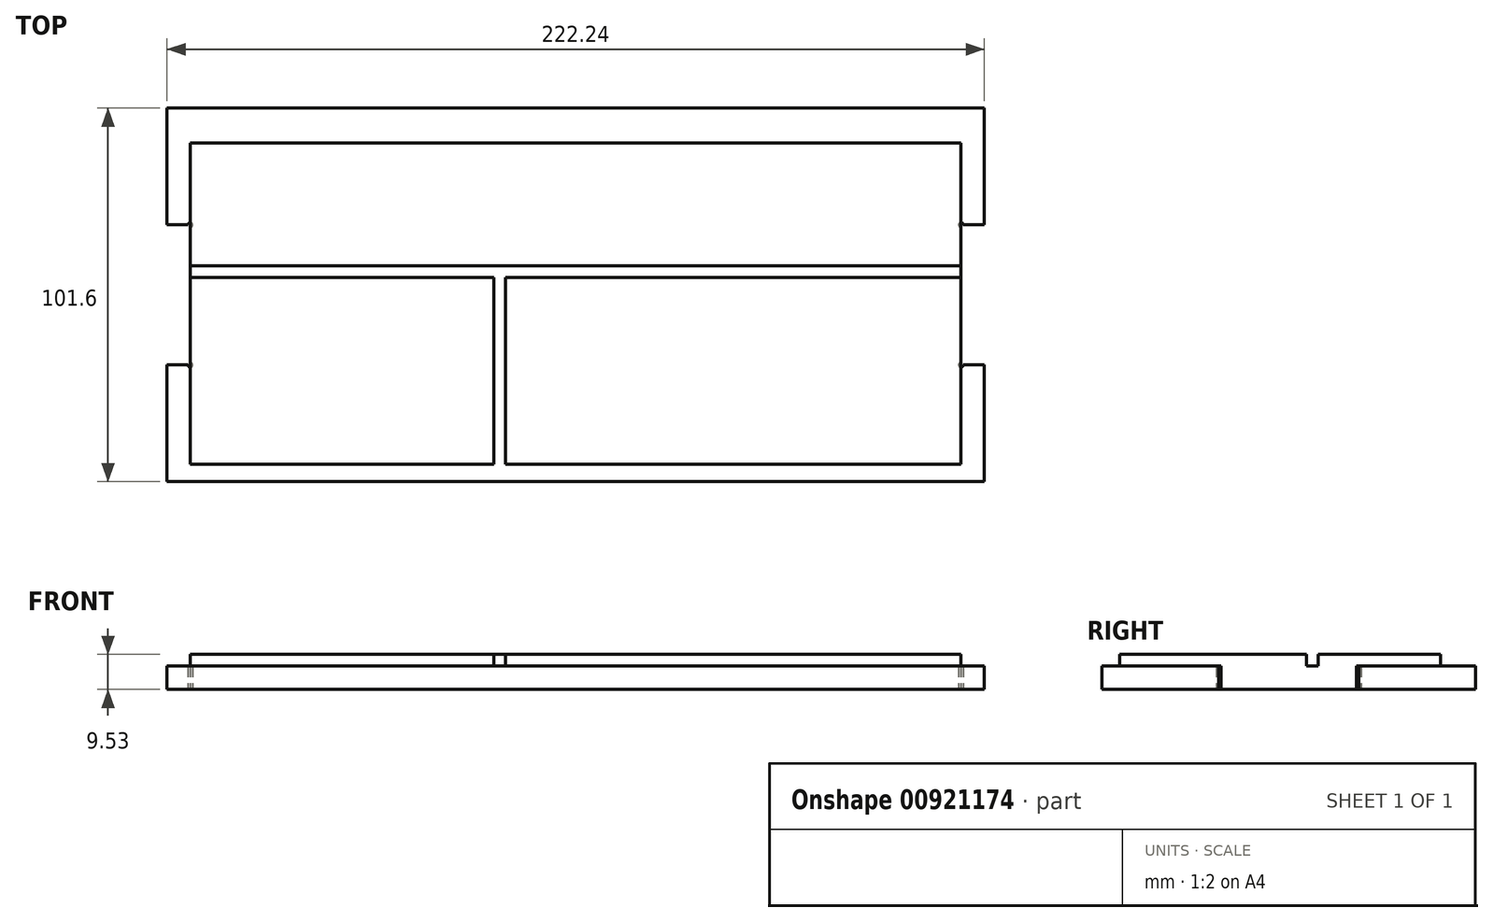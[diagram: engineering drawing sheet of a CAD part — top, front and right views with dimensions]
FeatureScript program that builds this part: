
annotation { "Feature Type Name" : "Feature", "Feature Type Description" : "" }
export const myFeature = defineFeature(function(context is Context, id is Id, definition is map)
    precondition{}
    {
        {
            var Q0;
            Q0=qCreatedBy(makeId("Top.planeOp"),FACE);
            var sketch = newSketch(context, id + "F0", { "sketchPlane" : qUnion([Q0])});
            skLineSegment(sketch, "E0.bottom", {"start": v(111.13, -50.8) * mm, "end": v(-111.12, -50.8) * mm});
            skLineSegment(sketch, "E0.top", {"start": v(111.12, 50.8) * mm, "end": v(-111.13, 50.8) * mm});
            skLineSegment(sketch, "E0.left", {"start": v(111.13, -50.8) * mm, "end": v(111.12, 50.8) * mm});
            skLineSegment(sketch, "E0.right", {"start": v(-111.12, -50.8) * mm, "end": v(-111.13, 50.8) * mm});
            skPoint(sketch, "E0.middle", {"position": v(0, 0) * mm});
            skSolve(sketch);
        }
        {
            var Q0;
            Q0=qSketchRegion(id+"F0",true);
            extrude(context, id + "F1", {"entities" : qUnion([Q0]), "depth" : 9.52 * mm, "offsetDistance" : 25.4 * mm});
        }
        {
            var Q0;
            Q0=makeQuery(id+"F1.opExtrude","CAP_FACE",FACE,{"disambiguationData":[OSD([sQuery(id+"F0.wireOp",EDGE,"E0.bottom"),sQuery(id+"F0.wireOp",EDGE,"E0.top"),sQuery(id+"F0.wireOp",EDGE,"E0.left"),sQuery(id+"F0.wireOp",EDGE,"E0.right")])],"isStart":false});
            var sketch = newSketch(context, id + "F2", { "sketchPlane" : qUnion([Q0])});
            skLineSegment(sketch, "E1.bottom", {"start": v(-111.13, 19.05) * mm, "end": v(-104.78, 19.05) * mm});
            skLineSegment(sketch, "E1.top", {"start": v(-111.13, -19.05) * mm, "end": v(-104.78, -19.05) * mm});
            skLineSegment(sketch, "E1.left", {"start": v(-111.13, 19.05) * mm, "end": v(-111.13, -19.05) * mm});
            skLineSegment(sketch, "E1.right", {"start": v(-104.78, 19.05) * mm, "end": v(-104.78, -19.05) * mm});
            skLineSegment(sketch, "E2.bottom", {"start": v(111.13, 19.05) * mm, "end": v(104.78, 19.05) * mm});
            skLineSegment(sketch, "E2.top", {"start": v(111.13, -19.05) * mm, "end": v(104.78, -19.05) * mm});
            skLineSegment(sketch, "E2.left", {"start": v(111.13, 19.05) * mm, "end": v(111.13, -19.05) * mm});
            skLineSegment(sketch, "E2.right", {"start": v(104.78, 19.05) * mm, "end": v(104.78, -19.05) * mm});
            skLineSegment(sketch, "E3", {"start": v(-111.13, 0) * mm, "end": v(111.12, 0) * mm, "construction": true});
            skSolve(sketch);
        }
        {
            var Q0;
            Q0=qSketchRegion(id+"F2",true);
            extrude(context, id + "F3", {"entities" : qUnion([Q0]), "operationType" : NewBodyOperationType.REMOVE, "endBound" : BoundingType.THROUGH_ALL, "oppositeDirection" : true, "depth" : 25.4 * mm, "offsetDistance" : 25.4 * mm});
        }
        {
            var Q0;
            Q0=makeQuery(id+"F1.opExtrude","CAP_FACE",FACE,{"disambiguationData":[OSD([sQuery(id+"F0.wireOp",EDGE,"E0.bottom"),sQuery(id+"F0.wireOp",EDGE,"E0.top"),sQuery(id+"F0.wireOp",EDGE,"E0.left"),sQuery(id+"F0.wireOp",EDGE,"E0.right")])],"isStart":false});
            var sketch = newSketch(context, id + "F4", { "sketchPlane" : qUnion([Q0])});
            skLineSegment(sketch, "E4", {"start": v(-104.78, 19.05) * mm, "end": v(-111.13, 19.05) * mm});
            skLineSegment(sketch, "E5", {"start": v(-111.13, 19.05) * mm, "end": v(-111.13, 50.8) * mm});
            skLineSegment(sketch, "E6", {"start": v(-111.13, 50.8) * mm, "end": v(111.12, 50.8) * mm});
            skLineSegment(sketch, "E7", {"start": v(111.12, 50.8) * mm, "end": v(111.12, 19.05) * mm});
            skLineSegment(sketch, "E8", {"start": v(111.12, 19.05) * mm, "end": v(104.78, 19.05) * mm});
            skLineSegment(sketch, "E9", {"start": v(104.78, 19.05) * mm, "end": v(104.78, 41.28) * mm});
            skLineSegment(sketch, "E10", {"start": v(104.78, 41.28) * mm, "end": v(-104.78, 41.28) * mm});
            skLineSegment(sketch, "E11", {"start": v(-104.78, 41.28) * mm, "end": v(-104.78, 19.05) * mm});
            skLineSegment(sketch, "E12", {"start": v(111.13, -19.05) * mm, "end": v(111.13, -50.8) * mm});
            skLineSegment(sketch, "E13", {"start": v(111.13, -50.8) * mm, "end": v(-111.12, -50.8) * mm});
            skLineSegment(sketch, "E14", {"start": v(-111.12, -50.8) * mm, "end": v(-111.12, -19.05) * mm});
            skLineSegment(sketch, "E15", {"start": v(-111.12, -19.05) * mm, "end": v(-104.78, -19.05) * mm});
            skLineSegment(sketch, "E16", {"start": v(-104.77, -19.05) * mm, "end": v(-104.77, -46.04) * mm});
            skLineSegment(sketch, "E17", {"start": v(-104.77, -46.04) * mm, "end": v(104.78, -46.04) * mm});
            skLineSegment(sketch, "E18", {"start": v(104.78, -46.04) * mm, "end": v(104.78, -19.05) * mm});
            skLineSegment(sketch, "E19", {"start": v(104.78, -19.05) * mm, "end": v(111.13, -19.05) * mm});
            skSolve(sketch);
        }
        {
            var Q0;
            Q0=makeQuery(id+"F4.imprint","IMPRINT",FACE,{"disambiguationData":[TD([[makeQuery(id+"F4.imprint","IMPRINT",EDGE,{"derivedFrom":sQuery(id+"F4.wireOp",EDGE,"E12")}),1.0]])]});
            var Q1;
            Q1=makeQuery(id+"F4.imprint","IMPRINT",FACE,{"disambiguationData":[TD([[makeQuery(id+"F4.imprint","IMPRINT",EDGE,{"derivedFrom":sQuery(id+"F4.wireOp",EDGE,"E4")}),1.0]])]});
            extrude(context, id + "F5", {"entities" : qUnion([Q0, Q1]), "operationType" : NewBodyOperationType.REMOVE, "oppositeDirection" : true, "depth" : 3.17 * mm, "offsetDistance" : 25.4 * mm});
        }
        {
            var Q0;
            Q0=makeQuery(id+"F1.opExtrude","CAP_FACE",FACE,{"disambiguationData":[OSD([sQuery(id+"F0.wireOp",EDGE,"E0.bottom"),sQuery(id+"F0.wireOp",EDGE,"E0.top"),sQuery(id+"F0.wireOp",EDGE,"E0.left"),sQuery(id+"F0.wireOp",EDGE,"E0.right")])],"isStart":false});
            var sketch = newSketch(context, id + "F6", { "sketchPlane" : qUnion([Q0])});
            skLineSegment(sketch, "E20.bottom", {"start": v(-104.78, 7.94) * mm, "end": v(104.78, 7.94) * mm});
            skLineSegment(sketch, "E20.top", {"start": v(-104.78, 4.76) * mm, "end": v(104.78, 4.76) * mm});
            skLineSegment(sketch, "E20.left", {"start": v(-104.78, 7.94) * mm, "end": v(-104.78, 4.76) * mm});
            skLineSegment(sketch, "E20.right", {"start": v(104.78, 7.94) * mm, "end": v(104.78, 4.76) * mm});
            skLineSegment(sketch, "E21", {"start": v(-19.05, 4.76) * mm, "end": v(-19.05, -46.04) * mm});
            skLineSegment(sketch, "E22", {"start": v(-22.22, -46.04) * mm, "end": v(-19.05, -46.04) * mm});
            skLineSegment(sketch, "E23", {"start": v(-22.22, -46.04) * mm, "end": v(-22.22, 4.76) * mm});
            skSolve(sketch);
        }
        {
            var Q0;
            Q0=qSketchRegion(id+"F6",true);
            extrude(context, id + "F7", {"entities" : qUnion([Q0]), "operationType" : NewBodyOperationType.REMOVE, "oppositeDirection" : true, "depth" : 3.17 * mm, "offsetDistance" : 25.4 * mm});
        }
        {
            var Q0;
            Q0=makeQuery(id+"F1.opExtrude","CAP_FACE",FACE,{"disambiguationData":[OSD([sQuery(id+"F0.wireOp",EDGE,"E0.bottom"),sQuery(id+"F0.wireOp",EDGE,"E0.top"),sQuery(id+"F0.wireOp",EDGE,"E0.left"),sQuery(id+"F0.wireOp",EDGE,"E0.right")])],"isStart":true});
            var sketch = newSketch(context, id + "F8", { "sketchPlane" : qUnion([Q0])});
            skArc(sketch, "E24", {"start": v(104.78, 18.42) * mm, "mid": v(104.33, 19.5) * mm, "end": v(105.4, 19.05) * mm});
            skArc(sketch, "E25", {"start": v(105.4, -19.05) * mm, "mid": v(104.33, -19.5) * mm, "end": v(104.78, -18.41) * mm});
            skArc(sketch, "E26", {"start": v(-105.4, -19.05) * mm, "mid": v(-104.33, -19.5) * mm, "end": v(-104.78, -18.41) * mm});
            skArc(sketch, "E27", {"start": v(-104.78, 18.41) * mm, "mid": v(-104.33, 19.5) * mm, "end": v(-105.4, 19.05) * mm});
            skLineSegment(sketch, "E28", {"start": v(-104.78, -19.05) * mm, "end": v(-104.78, -18.41) * mm});
            skLineSegment(sketch, "E29", {"start": v(-104.78, -19.05) * mm, "end": v(-105.4, -19.05) * mm});
            skLineSegment(sketch, "E30", {"start": v(-104.78, 19.05) * mm, "end": v(-105.4, 19.05) * mm});
            skLineSegment(sketch, "E31", {"start": v(-104.78, 19.05) * mm, "end": v(-104.78, 18.41) * mm});
            skLineSegment(sketch, "E32", {"start": v(104.78, -19.05) * mm, "end": v(104.78, -18.41) * mm});
            skLineSegment(sketch, "E33", {"start": v(104.78, -19.05) * mm, "end": v(105.4, -19.05) * mm});
            skLineSegment(sketch, "E34", {"start": v(104.78, 19.05) * mm, "end": v(104.78, 18.42) * mm});
            skLineSegment(sketch, "E35", {"start": v(104.78, 19.05) * mm, "end": v(105.4, 19.05) * mm});
            skSolve(sketch);
        }
        {
            var Q0;
            Q0 = qSketchRegion(id + "F8", true);
            var Q1;
            Q1=makeQuery(id+"F5.boolean.opBoolean","COPY",FACE,{"derivedFrom":makeQuery(id+"F5.opExtrude","CAP_FACE",FACE,{"disambiguationData":[OSD([sQuery(id+"F4.wireOp",EDGE,"E4"),sQuery(id+"F4.wireOp",EDGE,"E5"),sQuery(id+"F4.wireOp",EDGE,"E6"),sQuery(id+"F4.wireOp",EDGE,"E7"),sQuery(id+"F4.wireOp",EDGE,"E8"),sQuery(id+"F4.wireOp",EDGE,"E9"),sQuery(id+"F4.wireOp",EDGE,"E10"),sQuery(id+"F4.wireOp",EDGE,"E11")])],"isStart":false})});
            extrude(context, id + "F9", {"entities" : qUnion([Q0]), "operationType" : NewBodyOperationType.REMOVE, "endBound" : BoundingType.UP_TO_SURFACE, "oppositeDirection" : true, "depth" : 25.4 * mm, "endBoundEntityFace" : qUnion([Q1]), "offsetDistance" : 25.4 * mm});
        }
    });
